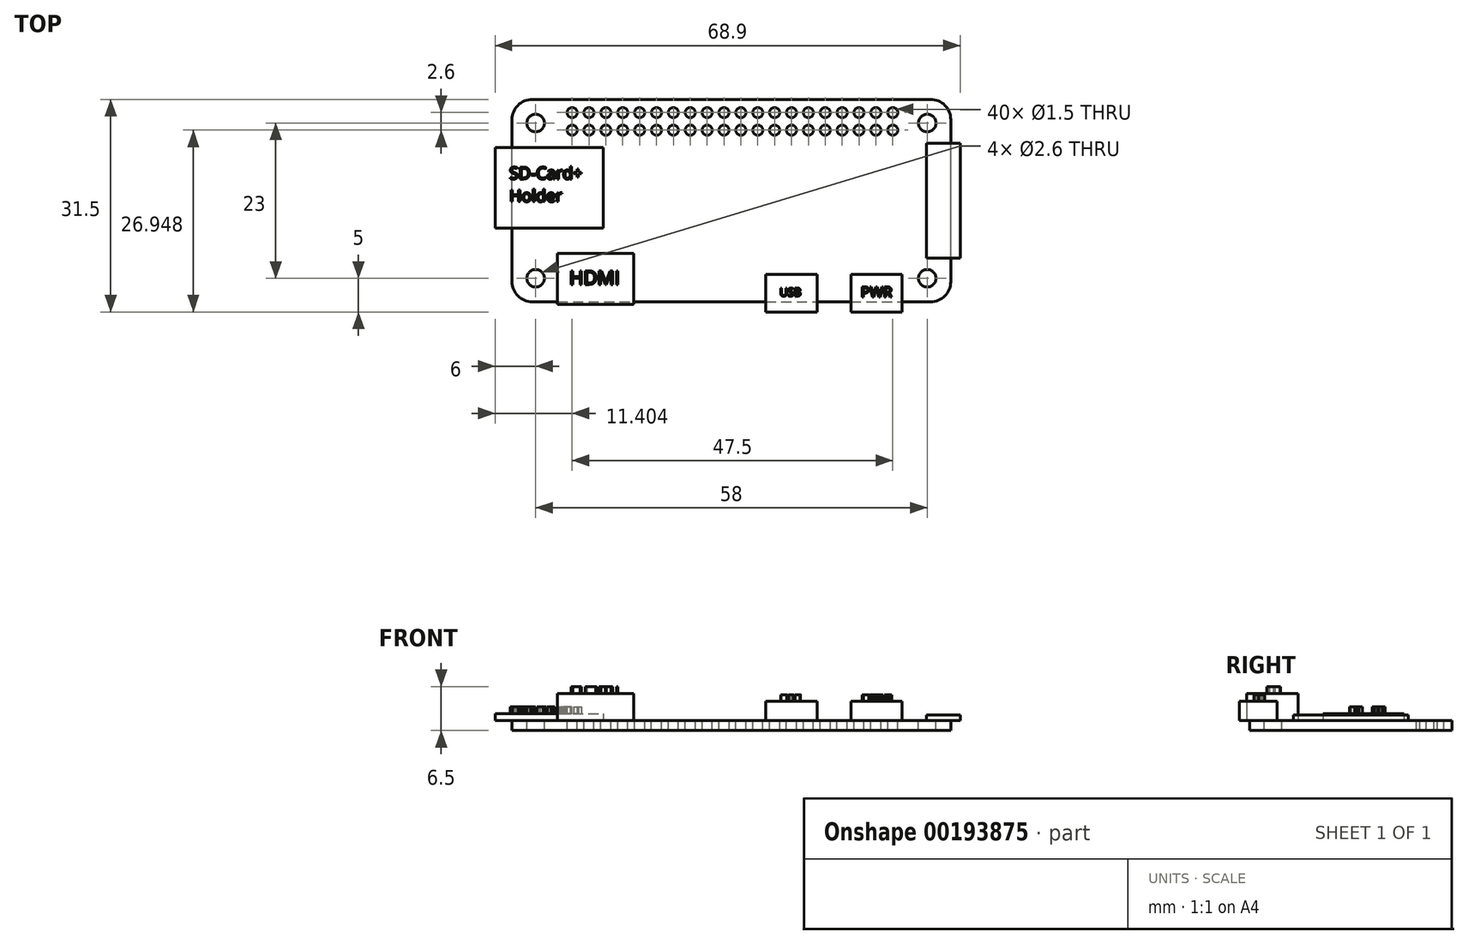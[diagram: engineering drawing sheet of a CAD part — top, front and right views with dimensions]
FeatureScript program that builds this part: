
annotation { "Feature Type Name" : "Feature", "Feature Type Description" : "" }
export const myFeature = defineFeature(function(context is Context, id is Id, definition is map)
    precondition{}
    {
        {
            var Q0;
            Q0=qCreatedBy(makeId("Top.planeOp"),FACE);
            var sketch = newSketch(context, id + "F0", { "sketchPlane" : qUnion([Q0])});
            skLineSegment(sketch, "E0.bottom", {"start": v(-32.5, -15) * mm, "end": v(32.5, -15) * mm});
            skLineSegment(sketch, "E0.top", {"start": v(-32.5, 15) * mm, "end": v(32.5, 15) * mm});
            skLineSegment(sketch, "E0.left", {"start": v(-32.5, -15) * mm, "end": v(-32.5, 15) * mm});
            skLineSegment(sketch, "E0.right", {"start": v(32.5, -15) * mm, "end": v(32.5, 15) * mm});
            skPoint(sketch, "E0.middle", {"position": v(0, 0) * mm});
            skSolve(sketch);
        }
        {
            var Q0;
            Q0 = qSketchRegion(id + "F0", true);
            extrude(context, id + "F1", {"entities" : qUnion([Q0]), "depth" : 1.5 * mm});
        }
        {
            var Q0;
            Q0=makeQuery(id+"F1.opExtrude","CAP_FACE",FACE,{"disambiguationData":[OSD([sQuery(id+"F0.wireOp",EDGE,"E0.bottom"),sQuery(id+"F0.wireOp",EDGE,"E0.top"),sQuery(id+"F0.wireOp",EDGE,"E0.left"),sQuery(id+"F0.wireOp",EDGE,"E0.right")])],"isStart":false});
            var sketch = newSketch(context, id + "F2", { "sketchPlane" : qUnion([Q0])});
            skCircle(sketch, "E1", {"center": v(-29, 11.5) * mm, "radius": 1.3 * mm});
            skCircle(sketch, "E2", {"center": v(29, 11.5) * mm, "radius": 1.3 * mm});
            skCircle(sketch, "E3", {"center": v(29, -11.5) * mm, "radius": 1.3 * mm});
            skCircle(sketch, "E4", {"center": v(-29, -11.5) * mm, "radius": 1.3 * mm});
            skSolve(sketch);
        }
        {
            var Q0;
            Q0 = qSketchRegion(id + "F2", true);
            extrude(context, id + "F3", {"entities" : qUnion([Q0]), "operationType" : NewBodyOperationType.REMOVE, "oppositeDirection" : true, "depth" : 25 * mm});
        }
        {
            var Q0;
            Q0=makeQuery(id+"F1.opExtrude","SWEPT_EDGE",EDGE,{"disambiguationData":[OSD([sQuery(id+"F0.wireOp",EDGE,"E0.top"),sQuery(id+"F0.wireOp",EDGE,"E0.left")])]});
            var Q1;
            Q1=makeQuery(id+"F1.opExtrude","SWEPT_EDGE",EDGE,{"disambiguationData":[OSD([sQuery(id+"F0.wireOp",EDGE,"E0.bottom"),sQuery(id+"F0.wireOp",EDGE,"E0.left")])]});
            var Q2;
            Q2=makeQuery(id+"F1.opExtrude","SWEPT_EDGE",EDGE,{"disambiguationData":[OSD([sQuery(id+"F0.wireOp",EDGE,"E0.top"),sQuery(id+"F0.wireOp",EDGE,"E0.right")])]});
            var Q3;
            Q3=makeQuery(id+"F1.opExtrude","SWEPT_EDGE",EDGE,{"disambiguationData":[OSD([sQuery(id+"F0.wireOp",EDGE,"E0.bottom"),sQuery(id+"F0.wireOp",EDGE,"E0.right")])]});
            fillet(context, id + "F4", {"entities" : qUnion([Q0, Q1, Q2, Q3]), "radius" : 3 * mm, "tangentPropagation" : true, "allowEdgeOverflow" : false});
        }
        {
            var Q0;
            Q0=makeQuery(id+"F1.opExtrude","CAP_FACE",FACE,{"disambiguationData":[OSD([sQuery(id+"F0.wireOp",EDGE,"E0.bottom"),sQuery(id+"F0.wireOp",EDGE,"E0.top"),sQuery(id+"F0.wireOp",EDGE,"E0.left"),sQuery(id+"F0.wireOp",EDGE,"E0.right")])],"isStart":false});
            var sketch = newSketch(context, id + "F5", { "sketchPlane" : qUnion([Q0])});
            skLineSegment(sketch, "E5.bottom", {"start": v(-25.75, -7.8) * mm, "end": v(-14.45, -7.8) * mm});
            skLineSegment(sketch, "E5.top", {"start": v(-25.75, -15.4) * mm, "end": v(-14.45, -15.4) * mm});
            skLineSegment(sketch, "E5.left", {"start": v(-25.75, -7.8) * mm, "end": v(-25.75, -15.4) * mm});
            skLineSegment(sketch, "E5.right", {"start": v(-14.45, -7.8) * mm, "end": v(-14.45, -15.4) * mm});
            skPoint(sketch, "E6", {"position": v(-20.1, -15.4) * mm});
            skSolve(sketch);
        }
        {
            var Q0;
            Q0 = qSketchRegion(id + "F5", true);
            extrude(context, id + "F6", {"entities" : qUnion([Q0]), "operationType" : NewBodyOperationType.ADD, "depth" : 4 * mm});
        }
        {
            var Q0;
            Q0=makeQuery(id+"F1.opExtrude","CAP_FACE",FACE,{"disambiguationData":[OSD([sQuery(id+"F0.wireOp",EDGE,"E0.bottom"),sQuery(id+"F0.wireOp",EDGE,"E0.top"),sQuery(id+"F0.wireOp",EDGE,"E0.left"),sQuery(id+"F0.wireOp",EDGE,"E0.right")])],"isStart":false});
            var sketch = newSketch(context, id + "F7", { "sketchPlane" : qUnion([Q0])});
            skLineSegment(sketch, "E7.bottom", {"start": v(5.1, -10.9) * mm, "end": v(12.7, -10.9) * mm});
            skLineSegment(sketch, "E7.top", {"start": v(5.1, -16.5) * mm, "end": v(12.7, -16.5) * mm});
            skLineSegment(sketch, "E7.left", {"start": v(5.1, -10.9) * mm, "end": v(5.1, -16.5) * mm});
            skLineSegment(sketch, "E7.right", {"start": v(12.7, -10.9) * mm, "end": v(12.7, -16.5) * mm});
            skLineSegment(sketch, "E8.bottom", {"start": v(17.7, -10.9) * mm, "end": v(25.3, -10.9) * mm});
            skLineSegment(sketch, "E8.top", {"start": v(17.7, -16.5) * mm, "end": v(25.3, -16.5) * mm});
            skLineSegment(sketch, "E8.left", {"start": v(17.7, -10.9) * mm, "end": v(17.7, -16.5) * mm});
            skLineSegment(sketch, "E8.right", {"start": v(25.3, -10.9) * mm, "end": v(25.3, -16.5) * mm});
            skPoint(sketch, "E9", {"position": v(8.9, -16.5) * mm});
            skPoint(sketch, "E10", {"position": v(21.5, -16.5) * mm});
            skSolve(sketch);
        }
        {
            var Q0;
            Q0 = qSketchRegion(id + "F7", true);
            extrude(context, id + "F8", {"entities" : qUnion([Q0]), "operationType" : NewBodyOperationType.ADD, "depth" : 2.8 * mm});
        }
        {
            var Q0;
            Q0=makeQuery(id+"F6.opExtrude","CAP_FACE",FACE,{"disambiguationData":[OSD([sQuery(id+"F5.wireOp",EDGE,"E5.bottom"),sQuery(id+"F5.wireOp",EDGE,"E5.top"),sQuery(id+"F5.wireOp",EDGE,"E5.left"),sQuery(id+"F5.wireOp",EDGE,"E5.right")])],"isStart":false});
            var sketch = newSketch(context, id + "F9", { "sketchPlane" : qUnion([Q0])});
            skText(sketch, "E11", { "text": "HDMI", "fontName": "OpenSans-Regular.ttf"});
            const initialGuessF9  = {"E11": [-0.024, -0.01242, 1, 0, 0.00203]};
            skSetInitialGuess(sketch, initialGuessF9);
            skSolve(sketch);
        }
        {
            var Q0;
            Q0 = qSketchRegion(id + "F9", true);
            extrude(context, id + "F10", {"entities" : qUnion([Q0]), "operationType" : NewBodyOperationType.ADD, "depth" : 1 * mm});
        }
        {
            var Q0;
            Q0=makeQuery(id+"F8.opExtrude","CAP_FACE",FACE,{"disambiguationData":[OSD([sQuery(id+"F7.wireOp",EDGE,"E7.bottom"),sQuery(id+"F7.wireOp",EDGE,"E7.top"),sQuery(id+"F7.wireOp",EDGE,"E7.left"),sQuery(id+"F7.wireOp",EDGE,"E7.right")])],"isStart":false});
            var sketch = newSketch(context, id + "F11", { "sketchPlane" : qUnion([Q0])});
            skText(sketch, "E12", { "text": "USB", "fontName": "OpenSans-Regular.ttf"});
            skText(sketch, "E13", { "text": "PWR", "fontName": "OpenSans-Regular.ttf"});
            const initialGuessF11  = {"E12": [0.00715, -0.01414, 1, 0, 0.00119], "E13": [0.01917, -0.01432, 1, 0, 0.00156]};
            skSetInitialGuess(sketch, initialGuessF11);
            skSolve(sketch);
        }
        {
            var Q0;
            Q0 = qSketchRegion(id + "F11", true);
            extrude(context, id + "F12", {"entities" : qUnion([Q0]), "operationType" : NewBodyOperationType.ADD, "depth" : 1 * mm});
        }
        {
            var Q0;
            Q0=makeQuery(id+"F1.opExtrude","CAP_FACE",FACE,{"disambiguationData":[OSD([sQuery(id+"F0.wireOp",EDGE,"E0.bottom"),sQuery(id+"F0.wireOp",EDGE,"E0.top"),sQuery(id+"F0.wireOp",EDGE,"E0.left"),sQuery(id+"F0.wireOp",EDGE,"E0.right")])],"isStart":false});
            var sketch = newSketch(context, id + "F13", { "sketchPlane" : qUnion([Q0])});
            skLineSegment(sketch, "E14.bottom", {"start": v(28.9, 8.5) * mm, "end": v(33.9, 8.5) * mm});
            skLineSegment(sketch, "E14.top", {"start": v(28.9, -8.5) * mm, "end": v(33.9, -8.5) * mm});
            skLineSegment(sketch, "E14.left", {"start": v(28.9, 8.5) * mm, "end": v(28.9, -8.5) * mm});
            skLineSegment(sketch, "E14.right", {"start": v(33.9, 8.5) * mm, "end": v(33.9, -8.5) * mm});
            skSolve(sketch);
        }
        {
            var Q0;
            Q0 = qSketchRegion(id + "F13", true);
            extrude(context, id + "F14", {"entities" : qUnion([Q0]), "operationType" : NewBodyOperationType.ADD, "depth" : 0.8 * mm});
        }
        {
            var Q0;
            Q0=makeQuery(id+"F1.opExtrude","CAP_FACE",FACE,{"disambiguationData":[OSD([sQuery(id+"F0.wireOp",EDGE,"E0.bottom"),sQuery(id+"F0.wireOp",EDGE,"E0.top"),sQuery(id+"F0.wireOp",EDGE,"E0.left"),sQuery(id+"F0.wireOp",EDGE,"E0.right")])],"isStart":false});
            var sketch = newSketch(context, id + "F15", { "sketchPlane" : qUnion([Q0])});
            skLineSegment(sketch, "E15.bottom", {"start": v(-35, 7.9) * mm, "end": v(-19, 7.9) * mm});
            skLineSegment(sketch, "E15.top", {"start": v(-35, -4.1) * mm, "end": v(-19, -4.1) * mm});
            skLineSegment(sketch, "E15.left", {"start": v(-35, 7.9) * mm, "end": v(-35, -4.1) * mm});
            skLineSegment(sketch, "E15.right", {"start": v(-19, 7.9) * mm, "end": v(-19, -4.1) * mm});
            skPoint(sketch, "E16", {"position": v(-35, 1.9) * mm});
            skSolve(sketch);
        }
        {
            var Q0;
            Q0 = qSketchRegion(id + "F15", true);
            extrude(context, id + "F16", {"entities" : qUnion([Q0]), "operationType" : NewBodyOperationType.ADD, "depth" : 1 * mm});
        }
        {
            var Q0;
            Q0=makeQuery(id+"F1.opExtrude","CAP_FACE",FACE,{"disambiguationData":[OSD([sQuery(id+"F0.wireOp",EDGE,"E0.bottom"),sQuery(id+"F0.wireOp",EDGE,"E0.top"),sQuery(id+"F0.wireOp",EDGE,"E0.left"),sQuery(id+"F0.wireOp",EDGE,"E0.right")])],"isStart":false});
            var sketch = newSketch(context, id + "F17", { "sketchPlane" : qUnion([Q0])});
            skLineSegment(sketch, "E17.bottom", {"start": v(0, 14.53) * mm, "end": v(25.5, 14.53) * mm});
            skLineSegment(sketch, "E17.top", {"start": v(-25.5, 9.03) * mm, "end": v(25.5, 9.03) * mm});
            skLineSegment(sketch, "E17.left", {"start": v(-25.5, 14.53) * mm, "end": v(-25.5, 9.03) * mm});
            skLineSegment(sketch, "E17.right", {"start": v(25.5, 14.53) * mm, "end": v(25.5, 9.03) * mm});
            skPoint(sketch, "E18", {"position": v(0, 14.53) * mm});
            skCircle(sketch, "E19.0", {"center": v(-29, 11.5) * mm, "radius": 1.3 * mm, "construction": true});
            skCircle(sketch, "E20", {"center": v(-23.6, 13.05) * mm, "radius": 0.75 * mm});
            skCircle(sketch, "E21.0.1.0", {"center": v(-23.6, 10.45) * mm, "radius": 0.75 * mm});
            skCircle(sketch, "E21.1.0.0", {"center": v(-21.1, 13.05) * mm, "radius": 0.75 * mm});
            skCircle(sketch, "E21.1.1.0", {"center": v(-21.1, 10.45) * mm, "radius": 0.75 * mm});
            skCircle(sketch, "E21.2.0.0", {"center": v(-18.6, 13.05) * mm, "radius": 0.75 * mm});
            skCircle(sketch, "E21.2.1.0", {"center": v(-18.6, 10.45) * mm, "radius": 0.75 * mm});
            skCircle(sketch, "E21.3.0.0", {"center": v(-16.1, 13.05) * mm, "radius": 0.75 * mm});
            skCircle(sketch, "E21.3.1.0", {"center": v(-16.1, 10.45) * mm, "radius": 0.75 * mm});
            skCircle(sketch, "E21.4.0.0", {"center": v(-13.6, 13.05) * mm, "radius": 0.75 * mm});
            skCircle(sketch, "E21.4.1.0", {"center": v(-13.6, 10.45) * mm, "radius": 0.75 * mm});
            skCircle(sketch, "E21.5.0.0", {"center": v(-11.1, 13.05) * mm, "radius": 0.75 * mm});
            skCircle(sketch, "E21.5.1.0", {"center": v(-11.1, 10.45) * mm, "radius": 0.75 * mm});
            skCircle(sketch, "E21.6.0.0", {"center": v(-8.6, 13.05) * mm, "radius": 0.75 * mm});
            skCircle(sketch, "E21.6.1.0", {"center": v(-8.6, 10.45) * mm, "radius": 0.75 * mm});
            skCircle(sketch, "E21.7.0.0", {"center": v(-6.1, 13.05) * mm, "radius": 0.75 * mm});
            skCircle(sketch, "E21.7.1.0", {"center": v(-6.1, 10.45) * mm, "radius": 0.75 * mm});
            skCircle(sketch, "E21.8.0.0", {"center": v(-3.6, 13.05) * mm, "radius": 0.75 * mm});
            skCircle(sketch, "E21.8.1.0", {"center": v(-3.6, 10.45) * mm, "radius": 0.75 * mm});
            skCircle(sketch, "E21.9.0.0", {"center": v(-1.1, 13.05) * mm, "radius": 0.75 * mm});
            skCircle(sketch, "E21.9.1.0", {"center": v(-1.1, 10.45) * mm, "radius": 0.75 * mm});
            skCircle(sketch, "E21.10.0.0", {"center": v(1.4, 13.05) * mm, "radius": 0.75 * mm});
            skCircle(sketch, "E21.10.1.0", {"center": v(1.4, 10.45) * mm, "radius": 0.75 * mm});
            skCircle(sketch, "E21.11.0.0", {"center": v(3.9, 13.05) * mm, "radius": 0.75 * mm});
            skCircle(sketch, "E21.11.1.0", {"center": v(3.9, 10.45) * mm, "radius": 0.75 * mm});
            skCircle(sketch, "E21.12.0.0", {"center": v(6.4, 13.05) * mm, "radius": 0.75 * mm});
            skCircle(sketch, "E21.12.1.0", {"center": v(6.4, 10.45) * mm, "radius": 0.75 * mm});
            skCircle(sketch, "E21.13.0.0", {"center": v(8.9, 13.05) * mm, "radius": 0.75 * mm});
            skCircle(sketch, "E21.13.1.0", {"center": v(8.9, 10.45) * mm, "radius": 0.75 * mm});
            skCircle(sketch, "E21.14.0.0", {"center": v(11.4, 13.05) * mm, "radius": 0.75 * mm});
            skCircle(sketch, "E21.14.1.0", {"center": v(11.4, 10.45) * mm, "radius": 0.75 * mm});
            skCircle(sketch, "E21.15.0.0", {"center": v(13.9, 13.05) * mm, "radius": 0.75 * mm});
            skCircle(sketch, "E21.15.1.0", {"center": v(13.9, 10.45) * mm, "radius": 0.75 * mm});
            skCircle(sketch, "E21.16.0.0", {"center": v(16.4, 13.05) * mm, "radius": 0.75 * mm});
            skCircle(sketch, "E21.16.1.0", {"center": v(16.4, 10.45) * mm, "radius": 0.75 * mm});
            skCircle(sketch, "E21.17.0.0", {"center": v(18.9, 13.05) * mm, "radius": 0.75 * mm});
            skCircle(sketch, "E21.17.1.0", {"center": v(18.9, 10.45) * mm, "radius": 0.75 * mm});
            skCircle(sketch, "E21.18.0.0", {"center": v(21.4, 13.05) * mm, "radius": 0.75 * mm});
            skCircle(sketch, "E21.18.1.0", {"center": v(21.4, 10.45) * mm, "radius": 0.75 * mm});
            skCircle(sketch, "E21.19.0.0", {"center": v(23.9, 13.05) * mm, "radius": 0.75 * mm});
            skCircle(sketch, "E21.19.1.0", {"center": v(23.9, 10.45) * mm, "radius": 0.75 * mm});
            skLineSegment(sketch, "E21.direction1", {"start": v(-23.6, 13.05) * mm, "end": v(-21.1, 13.05) * mm, "construction": true});
            skLineSegment(sketch, "E21.direction2", {"start": v(-23.6, 13.05) * mm, "end": v(-23.6, 10.45) * mm, "construction": true});
            skSolve(sketch);
        }
        {
            var Q0;
            Q0 = qSketchRegion(id + "F17", true);
            extrude(context, id + "F18", {"entities" : qUnion([Q0]), "operationType" : NewBodyOperationType.REMOVE, "oppositeDirection" : true, "depth" : 25 * mm});
        }
        {
            var Q0;
            Q0=makeQuery(id+"F16.opExtrude","CAP_FACE",FACE,{"disambiguationData":[OSD([sQuery(id+"F15.wireOp",EDGE,"E15.bottom"),sQuery(id+"F15.wireOp",EDGE,"E15.top"),sQuery(id+"F15.wireOp",EDGE,"E15.left"),sQuery(id+"F15.wireOp",EDGE,"E15.right")])],"isStart":false});
            var sketch = newSketch(context, id + "F19", { "sketchPlane" : qUnion([Q0])});
            skText(sketch, "E22", { "text": "SD-Card+\nHolder", "fontName": "OpenSans-Regular.ttf"});
            const initialGuessF19  = {"E22": [-0.0329, 0.0032, 1, 0, 0.00178]};
            skSetInitialGuess(sketch, initialGuessF19);
            skSolve(sketch);
        }
        {
            var Q0;
            Q0 = qSketchRegion(id + "F19", true);
            extrude(context, id + "F20", {"entities" : qUnion([Q0]), "operationType" : NewBodyOperationType.ADD, "depth" : 1 * mm});
        }
    });
